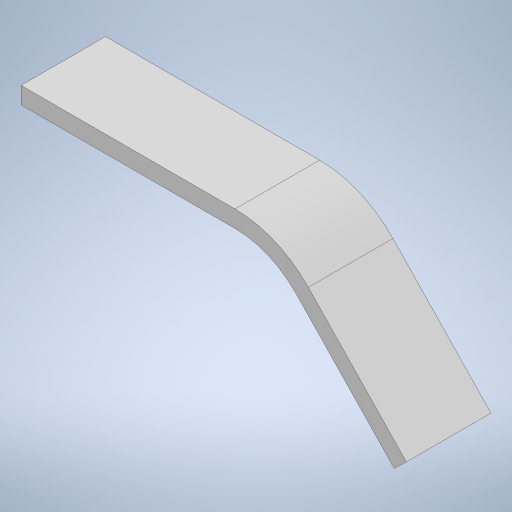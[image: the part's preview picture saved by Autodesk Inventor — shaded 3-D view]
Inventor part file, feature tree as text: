
AUTODESK INVENTOR PART (.ipt)
format: ipt  version: 2024.2 (Build 282272000, 272)  size: 219,648 bytes
history: native  units: in
note: dims shown in document units (in); Inventor stores cm internally (conversion verified against a paired STEP export)
features: sketch x2, sweep x1
ambient origin geometry x8: Origin, YZ Plane, XZ Plane, XY Plane, X Axis, Y Axis, Z Axis, Center Point
bodies: Solid1 (feature_tree)
feature tree (3):
  sweep  "Sweep1"
  sketch  "Sketch1"  dims[d0=0.75in d1=0.275in]
  sketch  "Sketch2"  dims[d2=0.05in d3=0.25in d4=0.0in d5=0.0in]
